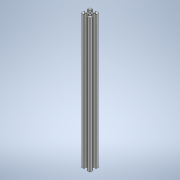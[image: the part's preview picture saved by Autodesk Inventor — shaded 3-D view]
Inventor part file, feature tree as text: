
AUTODESK INVENTOR PART (.ipt)
format: ipt  version: 2020 (Build 240168000, 168)  size: 274,432 bytes
history: native  units: mm
features: other x1, extrude x1, sketch x1
ambient origin geometry x8: Origin, YZ Plane, XZ Plane, XY Plane, X Axis, Y Axis, Z Axis, Center Point
bodies: Body1 (feature_tree)
feature tree (3):
  other  "Твердое тело1"
  extrude  "Выдавливание1"  Depth=0.25mm
  sketch  "Эскиз1"
